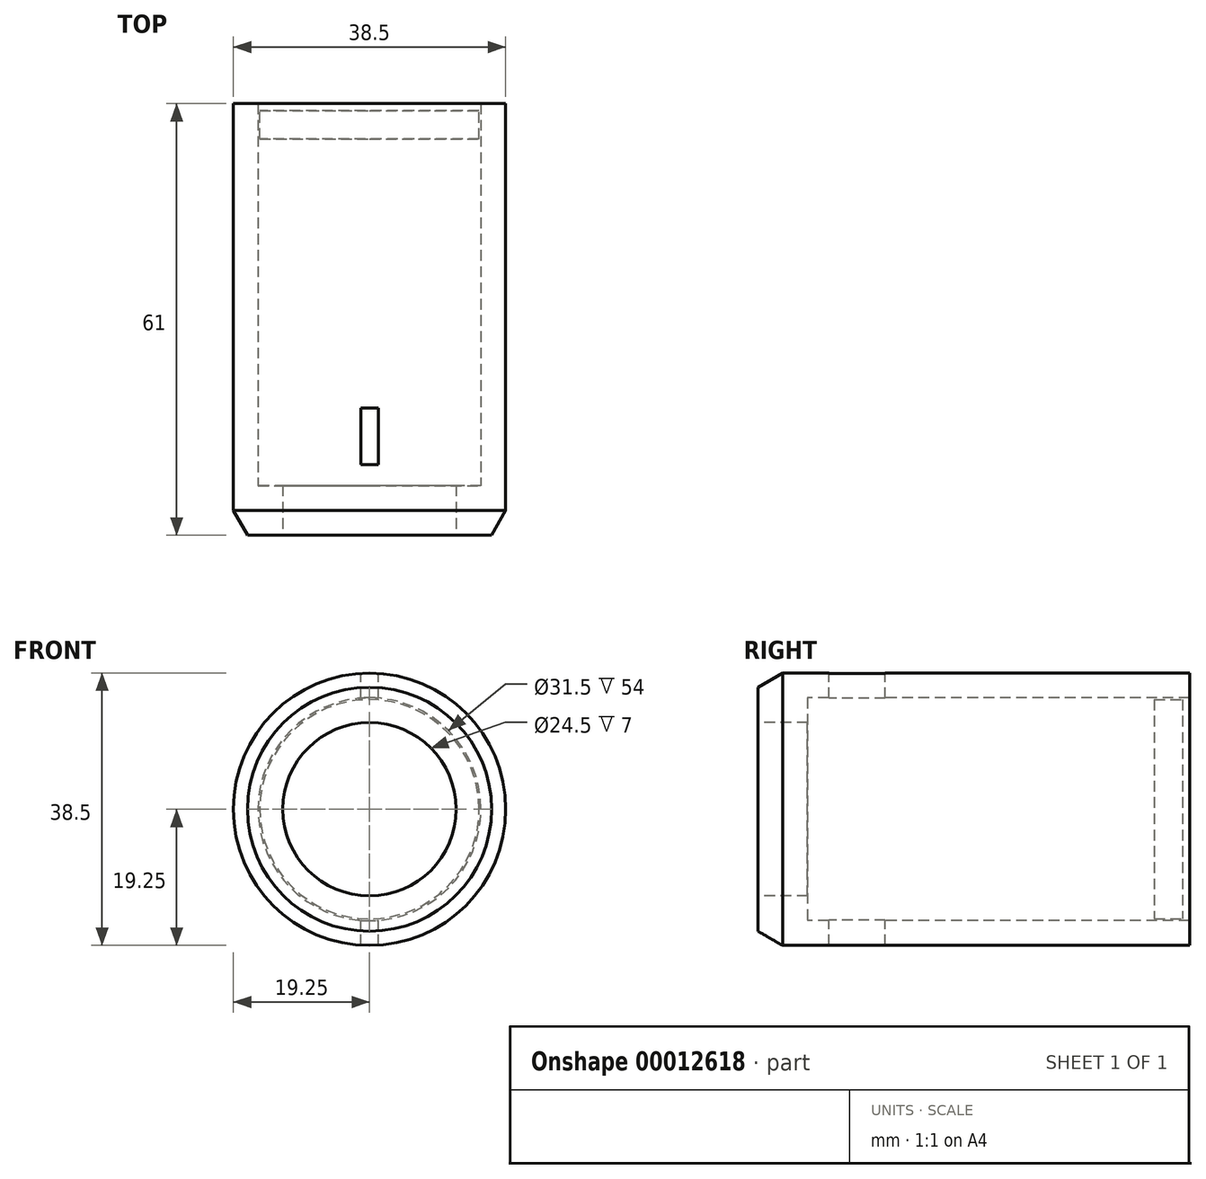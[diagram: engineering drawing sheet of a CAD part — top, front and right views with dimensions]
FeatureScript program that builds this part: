
annotation { "Feature Type Name" : "Feature", "Feature Type Description" : "" }
export const myFeature = defineFeature(function(context is Context, id is Id, definition is map)
    precondition{}
    {
        {
            var Q0;
            Q0=qCreatedBy(makeId("Front.planeOp"),FACE);
            var sketch = newSketch(context, id + "F0", { "sketchPlane" : qUnion([Q0])});
            skCircle(sketch, "E0", {"center": v(0, 0) * mm, "radius": 12.25 * mm});
            skCircle(sketch, "E1.0", {"center": v(0, 0) * mm, "radius": 19.25 * mm});
            skSolve(sketch);
        }
        {
            var Q0;
            Q0 = qSketchRegion(id + "F0", true);
            extrude(context, id + "F1", {"entities" : qUnion([Q0]), "oppositeDirection" : true, "depth" : 7 * mm});
        }
        {
            var Q0;
            Q0=makeQuery(id+"F1.opExtrude","CAP_FACE",FACE,{"disambiguationData":[OSD([sQuery(id+"F0.wireOp",EDGE,"E0"),sQuery(id+"F0.wireOp",EDGE,"E1.0")])],"isStart":false});
            var sketch = newSketch(context, id + "F2", { "sketchPlane" : qUnion([Q0])});
            skCircle(sketch, "E2.0", {"center": v(0, 0) * mm, "radius": 12.25 * mm});
            skCircle(sketch, "E3.0", {"center": v(0, 0) * mm, "radius": 19.25 * mm});
            skSolve(sketch);
        }
        {
            var Q0;
            Q0 = qSketchRegion(id + "F2", true);
            extrude(context, id + "F3", {"entities" : qUnion([Q0]), "operationType" : NewBodyOperationType.ADD, "oppositeDirection" : true, "depth" : 2 * mm});
        }
        {
            var Q0;
            Q0=makeQuery(id+"F3.boolean.opBoolean","MERGE",FACE,{"derivedFrom":[makeQuery(id+"F1.opExtrude","CAP_FACE",FACE,{"disambiguationData":[OSD([sQuery(id+"F0.wireOp",EDGE,"E0"),sQuery(id+"F0.wireOp",EDGE,"E1.0")])],"isStart":false}),makeQuery(id+"F3.opExtrude","CAP_FACE",FACE,{"disambiguationData":[OSD([sQuery(id+"F2.wireOp",EDGE,"d977d55e-f729-4752-8bf7-8e9448e0e988"),sQuery(id+"F2.wireOp",EDGE,"E2.0")])],"isStart":true})]});
            var sketch = newSketch(context, id + "F4", { "sketchPlane" : qUnion([Q0])});
            skCircle(sketch, "E4.0", {"center": v(0, 0) * mm, "radius": 15.75 * mm});
            skCircle(sketch, "E5.0", {"center": v(0, 0) * mm, "radius": 19.25 * mm});
            skSolve(sketch);
        }
        {
            var Q0;
            Q0=makeQuery(id+"F4.imprint","IMPRINT",FACE,{"disambiguationData":[TD([[makeQuery(id+"F4.imprint","IMPRINT",EDGE,{"derivedFrom":sQuery(id+"F4.wireOp",EDGE,"2abac362-f9e5-4cc8-9129-10381d22867c.0")}),1.0]])]});
            var Q1;
            Q1=makeQuery(id+"F4.imprint","IMPRINT",FACE,{"disambiguationData":[TD([[makeQuery(id+"F4.imprint","IMPRINT",EDGE,{"derivedFrom":sQuery(id+"F4.wireOp",EDGE,"E4.0")}),-1.0]])]});
            extrude(context, id + "F5", {"entities" : qUnion([Q0, Q1]), "operationType" : NewBodyOperationType.ADD, "depth" : 54 * mm});
        }
        {
            var Q0;
            Q0=makeQuery(id+"F1.opExtrude","CAP_EDGE",EDGE,{"disambiguationData":[OSD([sQuery(id+"F0.wireOp",EDGE,"E1.0")])],"isStart":true});
            chamfer(context, id + "F6", {"entities" : qUnion([Q0]), "chamferType" : ChamferType.OFFSET_ANGLE, "width" : 2 * mm, "oppositeDirection" : false, "angle" : 60 * degree, "tangentPropagation" : true});
        }
        {
            var Q0;
            Q0=makeQuery(id+"F5.opExtrude","CAP_FACE",FACE,{"disambiguationData":[OSD([sQuery(id+"F4.wireOp",EDGE,"E4.0"),sQuery(id+"F4.wireOp",EDGE,"E5.0")])],"isStart":false});
            cPlane(context, id + "F7", {"entities" : qUnion([Q0]), "cplaneType" : CPlaneType.OFFSET, "offset" : 1 * mm, "oppositeDirection" : true, "width" : 150 * mm, "height" : 150 * mm});
        }
        {
            var Q0;
            Q0=qCreatedBy(id+"F7.planeOp",FACE);
            var sketch = newSketch(context, id + "F8", { "sketchPlane" : qUnion([Q0])});
            skCircle(sketch, "E6.0", {"center": v(0, 0) * mm, "radius": 15.5 * mm});
            skSolve(sketch);
        }
        {
            var Q0;
            Q0=makeQuery(id+"F8.imprint","IMPRINT",FACE,{"disambiguationData":[TD([[makeQuery(id+"F8.imprint","IMPRINT",EDGE,{"derivedFrom":sQuery(id+"F8.wireOp",EDGE,"E6.0")}),1.0]])]});
            extrude(context, id + "F9", {"entities" : qUnion([Q0]), "oppositeDirection" : true, "depth" : 4 * mm});
        }
        {
            var Q0;
            Q0=qCreatedBy(makeId("Top.planeOp"),FACE);
            var sketch = newSketch(context, id + "F10", { "sketchPlane" : qUnion([Q0])});
            skLineSegment(sketch, "E7.0", {"start": v(-15.5, 56) * mm, "end": v(15.5, 56) * mm, "construction": true});
            skLineSegment(sketch, "E8", {"start": v(0, 56) * mm, "end": v(0, 59.58) * mm, "construction": true});
            skCircle(sketch, "E9", {"center": v(0, 58) * mm, "radius": 1 * mm});
            skSolve(sketch);
        }
        {
            var Q0;
            Q0=qCreatedBy(makeId("Top.planeOp"),FACE);
            var sketch = newSketch(context, id + "F11", { "sketchPlane" : qUnion([Q0])});
            skLineSegment(sketch, "E10.rect.bottom", {"start": v(1.25, 18) * mm, "end": v(-1.25, 18) * mm});
            skLineSegment(sketch, "E10.rect.top", {"start": v(1.25, 10) * mm, "end": v(-1.25, 10) * mm});
            skLineSegment(sketch, "E10.rect.left", {"start": v(1.25, 18) * mm, "end": v(1.25, 10) * mm});
            skLineSegment(sketch, "E10.rect.right", {"start": v(-1.25, 18) * mm, "end": v(-1.25, 10) * mm});
            skPoint(sketch, "E10.rect.middle", {"position": v(0, 14) * mm});
            skSolve(sketch);
        }
        {
            var Q0;
            Q0 = qSketchRegion(id + "F11", true);
            extrude(context, id + "F12", {"entities" : qUnion([Q0]), "operationType" : NewBodyOperationType.REMOVE, "oppositeDirection" : true, "depth" : 25 * mm, "hasSecondDirection" : true, "secondDirectionOppositeDirection" : false, "secondDirectionDepth" : 25 * mm});
        }
    });
